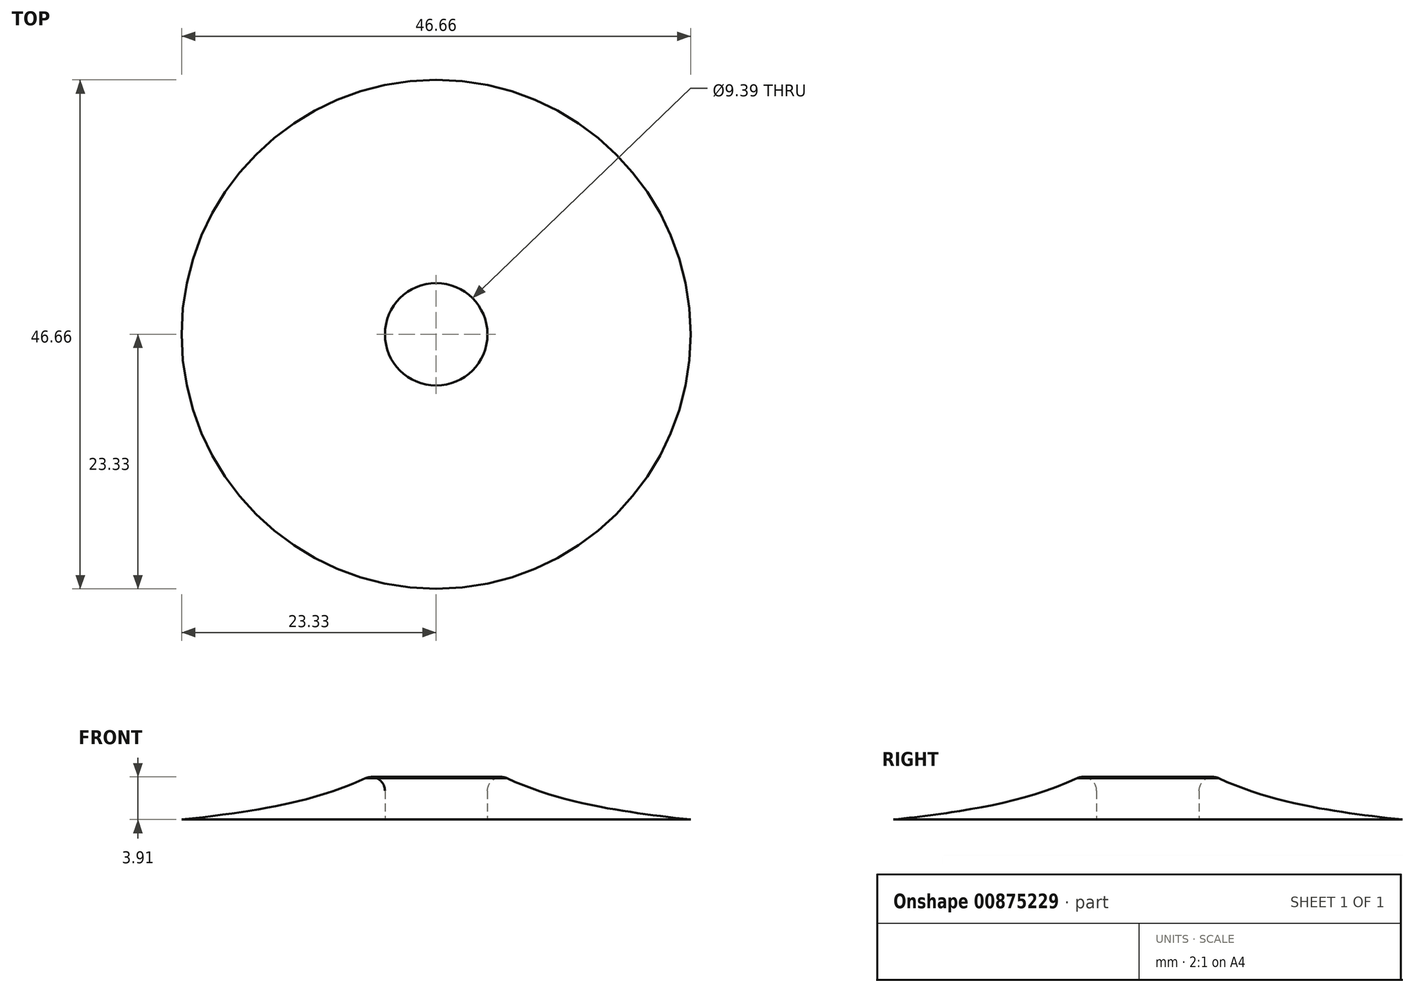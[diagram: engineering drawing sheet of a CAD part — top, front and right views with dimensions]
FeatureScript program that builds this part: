
annotation { "Feature Type Name" : "Feature", "Feature Type Description" : "" }
export const myFeature = defineFeature(function(context is Context, id is Id, definition is map)
    precondition{}
    {
        {
            var Q0;
            Q0=qCreatedBy(makeId("Front.planeOp"),FACE);
            var sketch = newSketch(context, id + "F0", { "sketchPlane" : qUnion([Q0])});
            skLineSegment(sketch, "E0", {"start": v(0, 0) * mm, "end": v(23.33, 0) * mm});
            skLineSegment(sketch, "E1", {"start": v(0, 0) * mm, "end": v(0, 7.88) * mm});
            skFitSpline(sketch, "E2", {"points": [v(0, 7.88) * mm, v(23.33, 0) * mm], "startDerivative": vector(19.02, -14.97) * mm, "endDerivative": vector(35, -3.72) * mm});
            skPoint(sketch, "E3", {"position": v(11.66, 0) * mm});
            skSolve(sketch);
        }
        {
            var Q0;
            Q0=makeQuery(id+"F0.imprint","IMPRINT",FACE,{"disambiguationData":[TD([[makeQuery(id+"F0.imprint","IMPRINT",EDGE,{"derivedFrom":sQuery(id+"F0.wireOp",EDGE,"E0")}),1.0]])]});
            var Q1;
            Q1=sQuery(id+"F0.wireOp",EDGE,"E1");
            revolve(context, id + "F1", {"surfaceOperationType" : NewSurfaceOperationType.NEW, "entities" : qUnion([Q0]), "axis" : qUnion([Q1]), "revolveType" : RevolveType.FULL});
        }
        {
            var Q0;
            Q0=qCreatedBy(makeId("Top.planeOp"),FACE);
            var sketch = newSketch(context, id + "F2", { "sketchPlane" : qUnion([Q0])});
            skCircle(sketch, "E4", {"center": v(0, 0) * mm, "radius": 4.7 * mm});
            skSolve(sketch);
        }
        {
            var Q0;
            Q0=makeQuery(id+"F2.imprint","IMPRINT",FACE,{"disambiguationData":[TD([[makeQuery(id+"F2.imprint","IMPRINT",EDGE,{"derivedFrom":sQuery(id+"F2.wireOp",EDGE,"E4")}),1.0]])]});
            extrude(context, id + "F3", {"entities" : qUnion([Q0]), "operationType" : NewBodyOperationType.REMOVE, "depth" : 25.4 * mm, "offsetDistance" : 25.4 * mm});
        }
        {
            var Q0;
            Q0=makeQuery(id+"F3.boolean.opBoolean","INTERSECT",EDGE,{"derivedFrom":[makeQuery(id+"F1.opRevolve","SWEPT_FACE",FACE,{"disambiguationData":[OSD([sQuery(id+"F0.wireOp",EDGE,"E2")])]}),makeQuery(id+"F3.opExtrude","SWEPT_FACE",FACE,{"disambiguationData":[OSD([sQuery(id+"F2.wireOp",EDGE,"E4")])]})]});
            fillet(context, id + "F4", {"entities" : qUnion([Q0]), "radius" : 1.27 * mm, "tangentPropagation" : true, "allowEdgeOverflow" : false});
        }
    });
